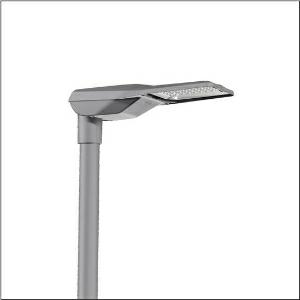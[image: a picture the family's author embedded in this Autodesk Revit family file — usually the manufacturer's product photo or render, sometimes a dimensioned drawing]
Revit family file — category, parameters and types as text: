
# Revit family: streetlight_sl_21_iq_mini___pl52_5xe2h41g08hb_e5d0
name_source: partatom
category: Lighting Fixtures
units: mm (PartAtom-declared; Revit-internal decimal feet)

## family parameters
Cut with Voids When Loaded = No
Host = Face
Light Source = No
Part Type = Normal
Room Calculation Point = No
Round Connector Dimension = Use Diameter
Shared = No

## types (1)
- --- (1 x LED, 9690 lm, 70.9 W, 4000K)
    Apparent Load = 71 VA
    CIE Flux Codes = 27 59 98 100 100
    Color Rendering = 70
    Color Temperature = 4000K
    Default Elevation = 1800 mm
    Description = Streetlight SL 21 mini, mast luminaire, primary light control with lens, of PMMA, primary optical cover: cover, of toughened safety glass, transparent, light distribution: PL52, light emission: direct distribution, primary light characteristic: asymmetric, installation type: post-top, side-entry, LED, High Power LED, rated luminous flux: 9.690lm, luminous efficacy: 137lm/W, light colour: 740, colour temperature: 4000K, control gear: ECG iQ, control: Street-Remote, Auto-Match, Temp-Guard, Lumen-Switch, Night-Set, Smart-Wire, Light-Fading, Desk-Remote (wireless, voltage-free reading and setting of iQ features in the workshop via application-optimized NFC function/RFID function), optimised constant luminous flux control (CLO 2.0), mains connection: 220..240V, AC, 50/60Hz, start of lifetime: 71W, end of lifetime: 75W, reduction: 31W, luminaire housing, of diecast aluminium, powder-coated, Siteco® metallic grey (DB 702S), corrosivity category C5 according to DIN EN ISO 12944, length: 628mm, width: 235mm, height: 110mm, spigot size: 60/76mm (post-top) and 42/60/76mm (side-entry), mast flange for spigot size: 42mm: 5XC10008XM4, 60mm: 5XC10008XM2, 76/60mm: 5XC10108XM1, protection rating (complete): IP66, insulation class (complete): insulation class II (safety insulation), certification: CE, ENEC, VDE, impact resistance: IK09, permissible operating ambient temperature for outdoor applications: -40..+50°C, standard-compliant lighting for roads and squares, packaging unit: 1 piece

Light Distribution: PL52
    Height = 110 mm
    Lamp = 1 x LED
    Lamp Light Flux = 9690 lm
    Lamp Power = 70.9 W
    Lamp count = 1
    Length = 625 mm
    Luminous efficacy = 137 lm/W
    Manufacturer = Siteco
    ModVariant = No
    Model = 5XE2H41G08HB
    Number of Poles = 1
    OnlyDefault = Yes
    Power Factor = 1
    Product Name = Streetlight SL 21 iQ mini | PL52
    Product group = mast luminaire | pylon top
    ProductGroupID = 6100
    Protection Class = Protection class II
    Protection Degree = IP 66
    RLX_Detail_Level = 1
    RlxData = <blob elided: 101801 chars, md5=93d85ba1>
    Socket = socket
    Standby Power = 0 W
    System Light Flux = 9690 lm
    System Power = 71 W
    Type Comments = factory setting: luminous flux: 100 % | dim-lin: 254 | 711 mA
    Type Image = l_1003519.jpg
    URL = http://relux.com
    VarID = @adj_069607
    Voltage = 0 V
    Weight = 0.00 kg
    Width = 234 mm

## geometry (parser evidence)
native form markers: Blend x4, Sweep x11
no freeform markers — native parametric forms only
